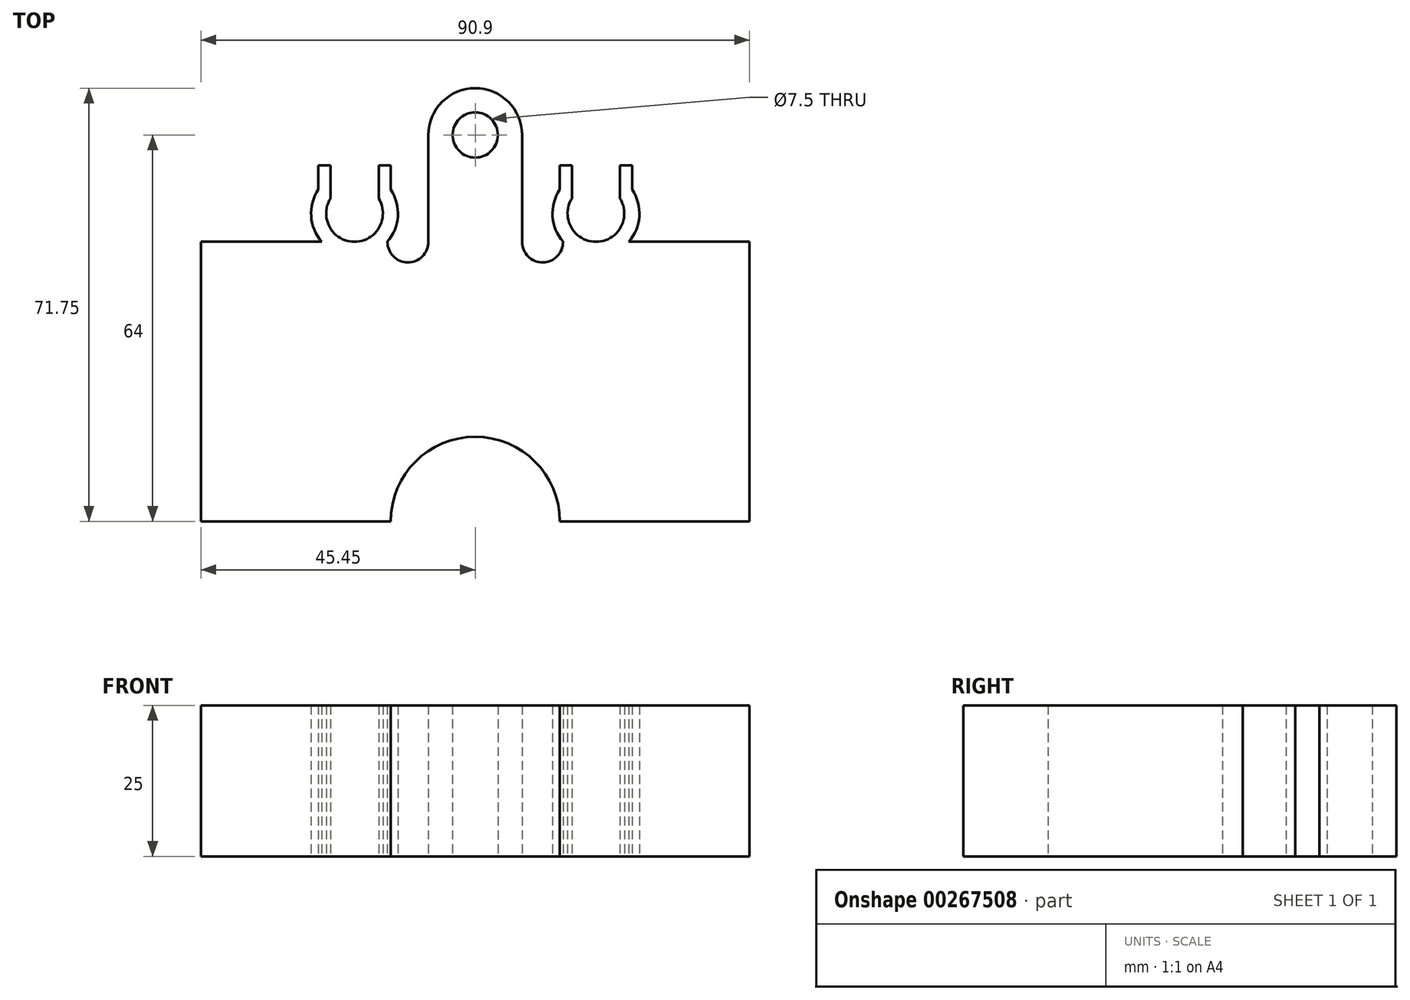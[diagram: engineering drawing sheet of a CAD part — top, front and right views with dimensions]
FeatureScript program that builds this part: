
annotation { "Feature Type Name" : "Feature", "Feature Type Description" : "" }
export const myFeature = defineFeature(function(context is Context, id is Id, definition is map)
    precondition{}
    {
        {
            var Q0;
            Q0=qCreatedBy(makeId("Top.planeOp"),FACE);
            var sketch = newSketch(context, id + "F0", { "sketchPlane" : qUnion([Q0])});
            skCircle(sketch, "E0", {"center": v(-20, 27) * mm, "radius": 4 * mm, "construction": true});
            skCircle(sketch, "E1", {"center": v(0, 40) * mm, "radius": 3.75 * mm});
            skArc(sketch, "E2", {"start": v(-14.55, 22.3) * mm, "mid": v(-11.15, 18.9) * mm, "end": v(-7.75, 22.3) * mm});
            skLineSegment(sketch, "E3", {"start": v(-7.75, 22.3) * mm, "end": v(-7.75, 40) * mm});
            skArc(sketch, "E4", {"start": v(0, 47.75) * mm, "mid": v(-5.48, 45.48) * mm, "end": v(-7.75, 40) * mm});
            skArc(sketch, "E5", {"start": v(-14.55, 22.3) * mm, "mid": v(-12.82, 26.54) * mm, "end": v(-14, 30.97) * mm});
            skLineSegment(sketch, "E6", {"start": v(-14, 30.97) * mm, "end": v(-16, 29.47) * mm, "construction": true});
            skArc(sketch, "E7", {"start": v(-20, 22.3) * mm, "mid": v(-15.9, 24.7) * mm, "end": v(-16, 29.47) * mm});
            skLineSegment(sketch, "E8", {"start": v(-20, 27) * mm, "end": v(-20, 22.3) * mm, "construction": true});
            skLineSegment(sketch, "E9", {"start": v(-20, 27) * mm, "end": v(-16, 29.47) * mm, "construction": true});
            skLineSegment(sketch, "E10.MirrorCS", {"start": v(-26, 30.97) * mm, "end": v(-24, 29.47) * mm, "construction": true});
            skArc(sketch, "E11.MirrorCS", {"start": v(-20, 22.3) * mm, "mid": v(-24.1, 24.7) * mm, "end": v(-24, 29.47) * mm});
            skArc(sketch, "E12.MirrorCS", {"start": v(-25.45, 22.3) * mm, "mid": v(-27.18, 26.54) * mm, "end": v(-26, 30.97) * mm});
            skLineSegment(sketch, "E13", {"start": v(-25.45, 22.3) * mm, "end": v(-45.45, 22.3) * mm});
            skLineSegment(sketch, "E14", {"start": v(-45.45, 22.3) * mm, "end": v(-45.45, -24) * mm});
            skLineSegment(sketch, "E15", {"start": v(-45.45, -24) * mm, "end": v(-14, -24) * mm});
            skArc(sketch, "E16", {"start": v(0, -10) * mm, "mid": v(-9.9, -14.1) * mm, "end": v(-14, -24) * mm});
            skLineSegment(sketch, "E17", {"start": v(-14, 30.97) * mm, "end": v(-14, 34.97) * mm});
            skLineSegment(sketch, "E18", {"start": v(-14, 34.97) * mm, "end": v(-16, 34.97) * mm});
            skLineSegment(sketch, "E19", {"start": v(-16, 34.97) * mm, "end": v(-16, 29.47) * mm});
            skLineSegment(sketch, "E20.MirrorCS", {"start": v(-24, 34.97) * mm, "end": v(-24, 29.47) * mm});
            skLineSegment(sketch, "E21.MirrorCS", {"start": v(-26, 34.97) * mm, "end": v(-24, 34.97) * mm});
            skLineSegment(sketch, "E22.MirrorCS", {"start": v(-26, 30.97) * mm, "end": v(-26, 34.97) * mm});
            skArc(sketch, "E23.MirrorCS", {"start": v(0, 47.75) * mm, "mid": v(5.48, 45.48) * mm, "end": v(7.75, 40) * mm});
            skLineSegment(sketch, "E24.MirrorCS", {"start": v(7.75, 22.3) * mm, "end": v(7.75, 40) * mm});
            skArc(sketch, "E25.MirrorCS", {"start": v(14.55, 22.3) * mm, "mid": v(11.15, 18.9) * mm, "end": v(7.75, 22.3) * mm});
            skArc(sketch, "E26.MirrorCS", {"start": v(14.55, 22.3) * mm, "mid": v(12.82, 26.54) * mm, "end": v(14, 30.97) * mm});
            skLineSegment(sketch, "E27.MirrorCS", {"start": v(14, 30.97) * mm, "end": v(14, 34.97) * mm});
            skLineSegment(sketch, "E28.MirrorCS", {"start": v(14, 34.97) * mm, "end": v(16, 34.97) * mm});
            skLineSegment(sketch, "E29.MirrorCS", {"start": v(16, 34.97) * mm, "end": v(16, 29.47) * mm});
            skArc(sketch, "E30.MirrorCS", {"start": v(20, 22.3) * mm, "mid": v(15.9, 24.7) * mm, "end": v(16, 29.47) * mm});
            skArc(sketch, "E31.MirrorCS", {"start": v(20, 22.3) * mm, "mid": v(24.1, 24.7) * mm, "end": v(24, 29.47) * mm});
            skLineSegment(sketch, "E32.MirrorCS", {"start": v(24, 34.97) * mm, "end": v(24, 29.47) * mm});
            skLineSegment(sketch, "E33.MirrorCS", {"start": v(26, 34.97) * mm, "end": v(24, 34.97) * mm});
            skArc(sketch, "E34.MirrorCS", {"start": v(25.45, 22.3) * mm, "mid": v(27.18, 26.54) * mm, "end": v(26, 30.97) * mm});
            skLineSegment(sketch, "E35.MirrorCS", {"start": v(25.45, 22.3) * mm, "end": v(45.45, 22.3) * mm});
            skLineSegment(sketch, "E36.MirrorCS", {"start": v(45.45, 22.3) * mm, "end": v(45.45, -24) * mm});
            skLineSegment(sketch, "E37.MirrorCS", {"start": v(45.45, -24) * mm, "end": v(14, -24) * mm});
            skArc(sketch, "E38.MirrorCS", {"start": v(0, -10) * mm, "mid": v(9.9, -14.1) * mm, "end": v(14, -24) * mm});
            skLineSegment(sketch, "E39.MirrorCS", {"start": v(26, 30.97) * mm, "end": v(26, 34.97) * mm});
            skSolve(sketch);
        }
        {
            var Q0;
            Q0 = qSketchRegion(id + "F0", true);
            extrude(context, id + "F1", {"entities" : qUnion([Q0]), "depth" : 25 * mm});
        }
    });
